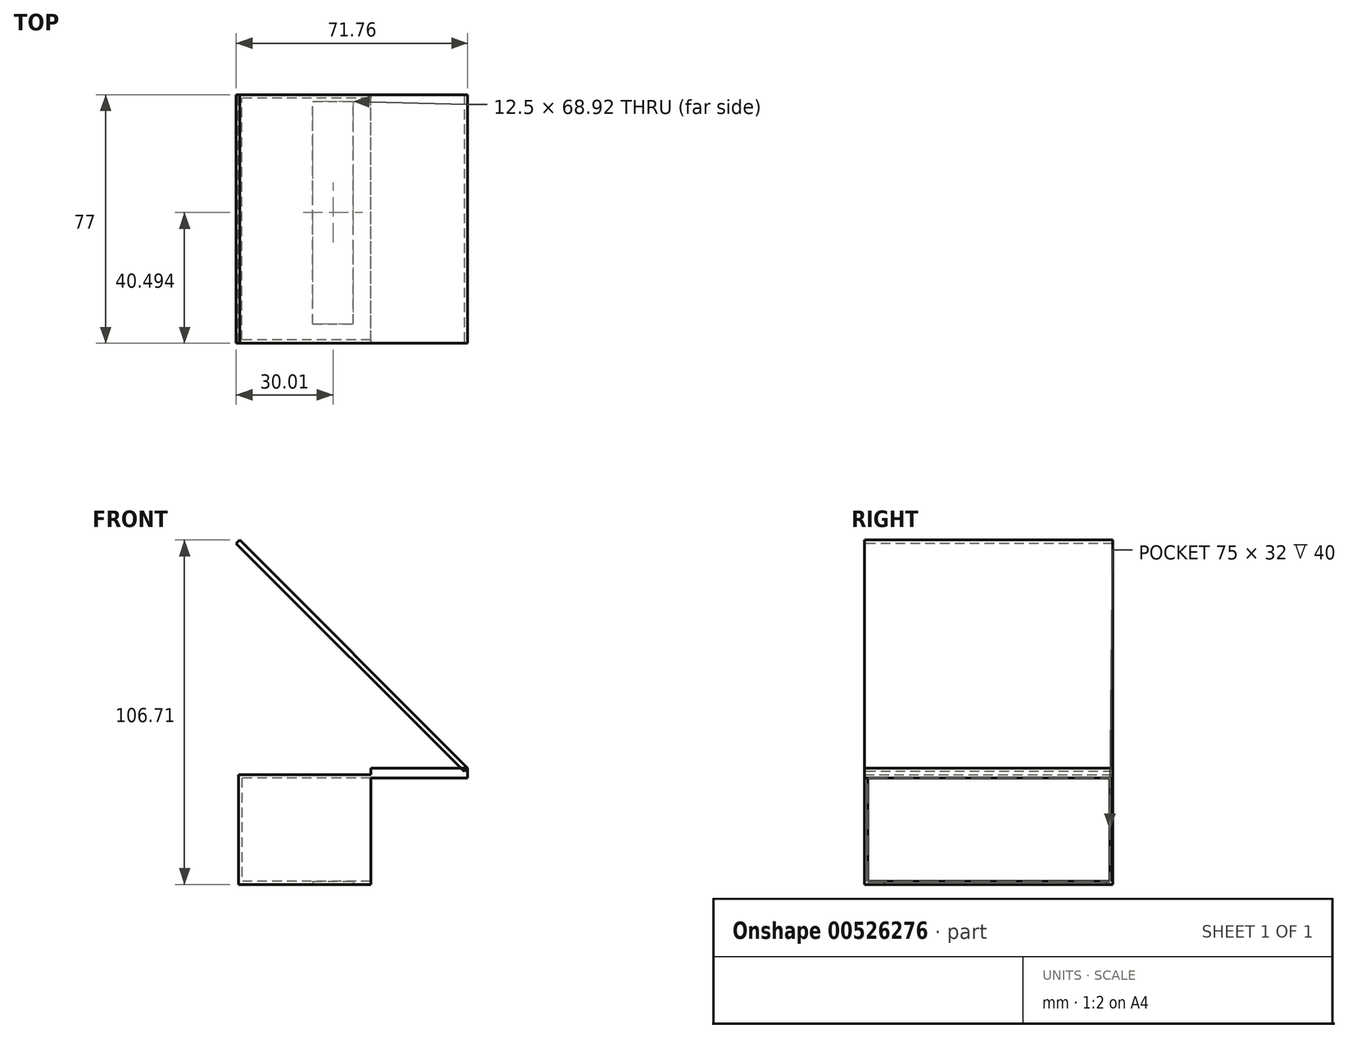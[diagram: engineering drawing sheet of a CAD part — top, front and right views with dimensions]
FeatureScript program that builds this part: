
annotation { "Feature Type Name" : "Feature", "Feature Type Description" : "" }
export const myFeature = defineFeature(function(context is Context, id is Id, definition is map)
    precondition{}
    {
        {
            var Q0;
            Q0=qCreatedBy(makeId("Right.planeOp"),FACE);
            var sketch = newSketch(context, id + "F0", { "sketchPlane" : qUnion([Q0])});
            skLineSegment(sketch, "E0.bottom", {"start": v(-46.76, 18.93) * mm, "end": v(28.24, 18.93) * mm});
            skLineSegment(sketch, "E0.top", {"start": v(-46.76, -13.07) * mm, "end": v(28.24, -13.07) * mm});
            skLineSegment(sketch, "E0.left", {"start": v(-46.76, 18.93) * mm, "end": v(-46.76, -13.07) * mm});
            skLineSegment(sketch, "E0.right", {"start": v(28.24, 18.93) * mm, "end": v(28.24, -13.07) * mm});
            skLineSegment(sketch, "E1.0", {"start": v(-47.76, 19.93) * mm, "end": v(29.24, 19.93) * mm});
            skLineSegment(sketch, "E1.1", {"start": v(-47.76, 19.93) * mm, "end": v(-47.76, -14.07) * mm});
            skLineSegment(sketch, "E1.2", {"start": v(-47.76, -14.07) * mm, "end": v(29.24, -14.07) * mm});
            skLineSegment(sketch, "E1.3", {"start": v(29.24, 19.93) * mm, "end": v(29.24, -14.07) * mm});
            skSolve(sketch);
        }
        {
            var Q0;
            Q0=makeQuery(id+"F0.imprint","IMPRINT",FACE,{"disambiguationData":[TD([[makeQuery(id+"F0.imprint","IMPRINT",EDGE,{"derivedFrom":sQuery(id+"F0.wireOp",EDGE,"E0.bottom")}),1.0]])]});
            extrude(context, id + "F1", {"entities" : qUnion([Q0]), "depth" : 40 * mm, "offsetDistance" : 25 * mm});
        }
        {
            var Q0;
            Q0=makeQuery(id+"F1.opExtrude","SWEPT_FACE",FACE,{"disambiguationData":[OSD([sQuery(id+"F0.wireOp",EDGE,"E1.2")])]});
            var sketch = newSketch(context, id + "F2", { "sketchPlane" : qUnion([Q0])});
            skLineSegment(sketch, "E2", {"start": v(0, 41.73) * mm, "end": v(40, 41.73) * mm});
            skLineSegment(sketch, "E3", {"start": v(0, -27.2) * mm, "end": v(40, -27.2) * mm});
            skLineSegment(sketch, "E4", {"start": v(22, 47.76) * mm, "end": v(22, -31.53) * mm});
            skLineSegment(sketch, "E5", {"start": v(34.5, 47.76) * mm, "end": v(34.5, -29.24) * mm});
            skSolve(sketch);
        }
        {
            var Q0;
            {var subQ0=sQuery(id+"F2.wireOp",EDGE,"E4");var subQ1=sQuery(id+"F2.wireOp",EDGE,"E2");var subQ2=makeQuery(id+"F2.imprint","INTERSECT",VERTEX,{"derivedFrom":[subQ1,subQ0]});Q0=makeQuery(id+"F2.imprint","IMPRINT",FACE,{"disambiguationData":[TD([[makeQuery(id+"F2.imprint","IMPRINT",EDGE,{"disambiguationData":[TD([[subQ2,-1.0]])],"derivedFrom":subQ1}),-1.0]])]});}
            extrude(context, id + "F3", {"entities" : qUnion([Q0]), "operationType" : NewBodyOperationType.REMOVE, "endBound" : BoundingType.UP_TO_NEXT, "oppositeDirection" : true, "depth" : 25 * mm, "offsetDistance" : 25 * mm});
        }
        {
            var Q0;
            Q0=makeQuery(id+"F1.opExtrude","CAP_FACE",FACE,{"disambiguationData":[OSD([sQuery(id+"F0.wireOp",EDGE,"E0.bottom"),sQuery(id+"F0.wireOp",EDGE,"E0.top"),sQuery(id+"F0.wireOp",EDGE,"E0.left"),sQuery(id+"F0.wireOp",EDGE,"E0.right"),sQuery(id+"F0.wireOp",EDGE,"E1.0"),sQuery(id+"F0.wireOp",EDGE,"E1.1"),sQuery(id+"F0.wireOp",EDGE,"E1.2"),sQuery(id+"F0.wireOp",EDGE,"E1.3")])],"isStart":true});
            var sketch = newSketch(context, id + "F4", { "sketchPlane" : qUnion([Q0])});
            skLineSegment(sketch, "E6.0", {"start": v(47.76, -14.07) * mm, "end": v(-29.24, -14.07) * mm});
            skLineSegment(sketch, "E7.0", {"start": v(47.76, 19.93) * mm, "end": v(47.76, -14.07) * mm});
            skLineSegment(sketch, "E8.0", {"start": v(47.76, 19.93) * mm, "end": v(-29.24, 19.93) * mm});
            skLineSegment(sketch, "E9.0", {"start": v(-29.24, 19.93) * mm, "end": v(-29.24, -14.07) * mm});
            skSolve(sketch);
        }
        {
            var Q0;
            Q0=makeQuery(id+"F4.imprint","IMPRINT",FACE,{"disambiguationData":[TD([[makeQuery(id+"F4.imprint","IMPRINT",EDGE,{"derivedFrom":sQuery(id+"F4.wireOp",EDGE,"E6.0")}),-1.0]])]});
            var Q1;
            Q1=makeQuery(id+"F4.imprint","IMPRINT",FACE,{"disambiguationData":[TD([[makeQuery(id+"F4.imprint","IMPRINT",EDGE,{"derivedFrom":makeQuery(id+"F1.opExtrude","CAP_EDGE",EDGE,{"disambiguationData":[OSD([sQuery(id+"F0.wireOp",EDGE,"E0.bottom")])],"isStart":true})}),1.0]])]});
            extrude(context, id + "F5", {"entities" : qUnion([Q0, Q1]), "operationType" : NewBodyOperationType.ADD, "depth" : 1 * mm, "offsetDistance" : 25 * mm});
        }
        {
            var Q0;
            Q0=makeQuery(id+"F1.opExtrude","CAP_FACE",FACE,{"disambiguationData":[OSD([sQuery(id+"F0.wireOp",EDGE,"E0.bottom"),sQuery(id+"F0.wireOp",EDGE,"E0.top"),sQuery(id+"F0.wireOp",EDGE,"E0.left"),sQuery(id+"F0.wireOp",EDGE,"E0.right"),sQuery(id+"F0.wireOp",EDGE,"E1.0"),sQuery(id+"F0.wireOp",EDGE,"E1.1"),sQuery(id+"F0.wireOp",EDGE,"E1.2"),sQuery(id+"F0.wireOp",EDGE,"E1.3")])],"isStart":false});
            var sketch = newSketch(context, id + "F6", { "sketchPlane" : qUnion([Q0])});
            skLineSegment(sketch, "E10", {"start": v(29.24, 21.93) * mm, "end": v(-47.76, 21.93) * mm});
            skLineSegment(sketch, "E11", {"start": v(29.24, 18.93) * mm, "end": v(-47.76, 18.93) * mm});
            skLineSegment(sketch, "E12", {"start": v(-47.76, 18.93) * mm, "end": v(-47.76, 21.93) * mm});
            skLineSegment(sketch, "E13", {"start": v(29.24, 18.93) * mm, "end": v(29.24, 21.93) * mm});
            skSolve(sketch);
        }
        {
            var Q0;
            {var subQ0=sQuery(id+"F6.wireOp",EDGE,"E10");Q0=makeQuery(id+"F6.imprint","IMPRINT",FACE,{"disambiguationData":[TD([[makeQuery(id+"F6.imprint","IMPRINT",EDGE,{"derivedFrom":subQ0}),1.0]])]});}
            var Q1;
            {var subQ1=makeQuery(id+"F1.opExtrude","CAP_EDGE",EDGE,{"disambiguationData":[OSD([sQuery(id+"F0.wireOp",EDGE,"E1.0")])],"isStart":false});Q1=makeQuery(id+"F6.imprint","IMPRINT",FACE,{"disambiguationData":[TD([[makeQuery(id+"F6.imprint","IMPRINT",EDGE,{"derivedFrom":subQ1}),-1.0]])]});}
            extrude(context, id + "F7", {"entities" : qUnion([Q0, Q1]), "operationType" : NewBodyOperationType.ADD, "depth" : 30 * mm, "offsetDistance" : 25 * mm});
        }
        {
            var Q0;
            Q0=makeQuery(id+"F7.opExtrude","SWEPT_FACE",FACE,{"disambiguationData":[OSD([sQuery(id+"F6.wireOp",EDGE,"E10")])]});
            var sketch = newSketch(context, id + "F8", { "sketchPlane" : qUnion([Q0])});
            skLineSegment(sketch, "E14.bottom", {"start": v(70, 29.24) * mm, "end": v(68.5, 29.24) * mm});
            skLineSegment(sketch, "E14.top", {"start": v(70, -47.76) * mm, "end": v(68.5, -47.76) * mm});
            skLineSegment(sketch, "E14.left", {"start": v(70, 29.24) * mm, "end": v(70, -47.76) * mm});
            skLineSegment(sketch, "E14.right", {"start": v(68.5, 29.24) * mm, "end": v(68.5, -47.76) * mm});
            skSolve(sketch);
        }
        {
            var Q0;
            Q0=makeQuery(id+"F8.imprint","IMPRINT",FACE,{"disambiguationData":[TD([[makeQuery(id+"F8.imprint","IMPRINT",EDGE,{"derivedFrom":sQuery(id+"F8.wireOp",EDGE,"E14.bottom")}),1.0]])]});
            extrude(context, id + "F9", {"entities" : qUnion([Q0]), "depth" : 100 * mm, "offsetDistance" : 25 * mm});
        }
        {
            var Q0;
            Q0=makeQuery(id+"F9.opExtrude","SWEPT_BODY",BODY,{"disambiguationData":[OSD([sQuery(id+"F8.wireOp",EDGE,"E14.bottom"),sQuery(id+"F8.wireOp",EDGE,"E14.top"),sQuery(id+"F8.wireOp",EDGE,"E14.left"),sQuery(id+"F8.wireOp",EDGE,"E14.right")])]});
            var Q1;
            Q1=makeQuery(id+"F7.opExtrude","CAP_EDGE",EDGE,{"disambiguationData":[OSD([sQuery(id+"F6.wireOp",EDGE,"E10")])],"isStart":false});
            transform(context, id + "F10", {"entities" : qUnion([Q0]), "transformType" : TransformType.ROTATION, "transformAxis" : qUnion([Q1]), "angle" : 45 * degree, "makeCopy" : false});
        }
    });
